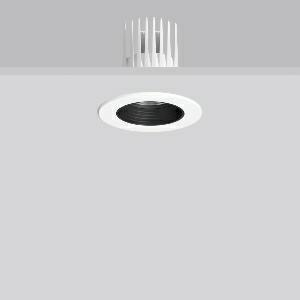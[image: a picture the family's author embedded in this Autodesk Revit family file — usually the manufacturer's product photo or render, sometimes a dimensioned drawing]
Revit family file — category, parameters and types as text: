
# Revit family: heledon_mini_e_901746_002_76_4a87
name_source: partatom
category: Lighting Fixtures
units: mm (PartAtom-declared; Revit-internal decimal feet)

## family parameters
Cut with Voids When Loaded = No
Host = Face
Light Source = No
Part Type = Normal
Room Calculation Point = No
Round Connector Dimension = Use Diameter
Shared = No

## types (1)
- HELEDON mini E (1 x LED Modul 930, 2250 lm, 3000)
    Apparent Load = 20 VA
    Approval mark = CE
    CIE Flux Codes = 80 99 100 100 100
    Color Rendering = 90
    Color Temperature = 3000
    Default Elevation = 1800 mm
    Description = Series: HELEDON mini
Round recessed downlight. Housing: die-cast aluminium, powder-coated. Black plastic ring and recessed LED to prevent glare from the side. Optical assembly with lens made of plastic (polycarbonate) for the best homogeneous light distribution - can be changed without tools. Best colour rendering index Ra>90. Suitable for Recessed ceiling mounting. Installation without tools thanks to spring fastening system. Including separate LED converter with connecting cable 600 mm.High quality converter without flickering and stroboscopic effect. Through-wiring box (5 pole) available as accessory. The following accessories can be mounted without use of tools: interchangeable lenses, decorative glasses, honeycomb louvre, clear and frosted diffusers, white interchangeable plastic ring. 
Colour: traffic white, matt (RAL 9016)
Diameter: 124 mm
Height: 3 mm
Cut-out diameter: 114 mm
Recess height: 170 mm
Luminaire: recess height: 120 mm
Lamp: LED
Socket: without socket
Colour temperature: 3000K
Colour rendering index (CRI): 92
System power: 20 W
Rated luminous flux: 2250 lm
Luminous efficiency: 113 lm/W
Control gear: Converter, dimmable, DALI
Protection class: II
Type of protection: IP 20
    Height = 0 mm  [stored 0 ft]
    Lamp = 1 x LED Modul 930
    Lamp Light Flux = 2250 lm
    Lamp count = 1
    Length = 124 mm  [stored 0.406824 ft]
    Lifetime = 50000 h
    Luminous efficacy = 113 lm/W
    Manufacturer = RZB
    ModVariant = No
    Model = 901746.002.76
    Mounting Place = Ceiling
    Mounting Type = Recessed
    Number of Poles = 1
    OnlyDefault = Yes
    Power Factor = 1
    Product Name = HELEDON mini E
    Product group = Recessed downlights
    ProductGroupID = 402
    Protection Class = Protection class II
    Protection Degree = IP 20
    RLX_Detail_Level = 1
    RLX_Emergency_Light_Flux = 0 lm
    RLX_Emergency_Type = 0
    RLX_Emergency_Type_DB = No
    RlxData = <blob elided: 127525 chars, md5=d667ef5b>
    Socket = socket
    Standby Power = 0 W
    System Light Flux = 2250 lm
    System Power = 20 W
    Type Comments = Product without accessories
    Type Image = 901656.002.jpg
    URL = http://relux.com
    VarID = ---
    Voltage = 230 V
    Voltage Range = 220-240 V
    Weight = 0.00 kg
    Width = 0 mm  [stored 0 ft]

note: [stored X ft] marks values corroborated as IEEE doubles in the binary element streams (Revit-internal decimal feet)

## geometry (parser evidence)
native form markers: Blend x4, Sweep x11
no freeform markers — native parametric forms only
